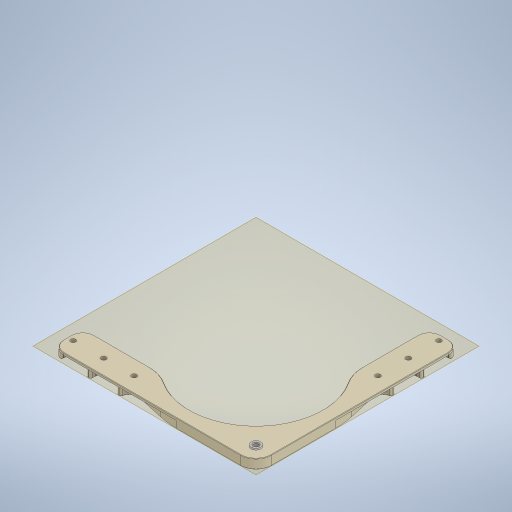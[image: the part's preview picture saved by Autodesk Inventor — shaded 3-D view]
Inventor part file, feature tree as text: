
AUTODESK INVENTOR PART (.ipt)
format: ipt  version: 2023.3 (Build 273359000, 359)  size: 1,759,744 bytes
history: native  units: in
note: dims shown in document units (in); Inventor stores cm internally (conversion verified against a paired STEP export)
features: other x16, chamfer x3, plane x1
ambient origin geometry x8: Origin, YZ Plane, XZ Plane, XY Plane, X Axis, Y Axis, Z Axis, Center Point
bodies: Solid1 (feature_tree), Solid2 (feature_tree), Solid3 (feature_tree), Solid4 (feature_tree), Solid5 (feature_tree), Solid6 (feature_tree), Solid7 (feature_tree), Solid8 (feature_tree), Solid9 (feature_tree), Solid10 (feature_tree), Solid11 (feature_tree), Solid12 (feature_tree), Solid13 (feature_tree), Solid14 (feature_tree), Solid15 (feature_tree), Solid16 (feature_tree), Solid17 (feature_tree), Solid18 (feature_tree), Solid19 (feature_tree)
feature tree (20):
  plane  "Work Plane1"
  other  "Boss-Extrude4[1]"
  other  "Boss-Extrude4[2]"
  other  "Boss-Extrude4[3]"
  other  "Boss-Extrude6[1]"
  other  "Boss-Extrude6[2]"
  other  "Boss-Extrude6[3]"
  other  "Boss-Extrude6[4]"
  other  "Boss-Extrude6[5]"
  other  "Boss-Extrude6[6]"
  other  "Boss-Extrude6[7]"
  other  "Boss-Extrude6[8]"
  other  "Boss-Extrude9[1]"
  other  "Boss-Extrude17[1]"
  other  "Boss-Extrude17[2]"
  other  "Boss-Extrude17[3]"
  chamfer  "Chamfer4"  [1 undecoded]
  other  "Move Face1"
  chamfer  "Chamfer1"  [1 undecoded]
  chamfer  "Chamfer2"  [1 undecoded]
note: 3 required parameter values undecoded (feature->parameter linkage not recoverable at this tier; creation-order binding heuristic only, values carry confidence <= 0.55)
